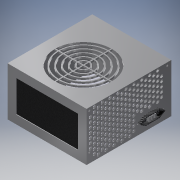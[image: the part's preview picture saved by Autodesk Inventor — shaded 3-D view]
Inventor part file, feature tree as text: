
AUTODESK INVENTOR PART (.ipt)
format: ipt  version: 2018.3 (Build 223284000, 284)  size: 2,151,424 bytes
history: native  units: mm
features: other x10, extrude x9, sketch x9, shell x1
ambient origin geometry x8: Origin, YZ Plane, XZ Plane, XY Plane, X Axis, Y Axis, Z Axis, Center Point
bodies: Solido1 (feature_tree)
feature tree (29):
  extrude  "Estrusione1"  Depth=140.0mm
  shell  "Svuotamento1"  Thickness=0.0mm
  extrude  "Estrusione2"  Depth=150.0mm
  extrude  "Estrusione3"  Depth=86.0mm TaperAngle=0.0deg
  extrude  "Estrusione4"  Depth=3.0mm
  extrude  "Estrusione5"  Depth=15.0mm
  extrude  "Estrusione6"  Depth=3.0mm TaperAngle=0.0deg
  extrude  "Estrusione7"  Depth=3.0mm
  extrude  "Estrusione8"  Depth=100.0mm
  extrude  "Estrusione9"  Depth=20.0mm
  sketch  "Schizzo1"
  sketch  "Schizzo3"
  other  "Linea chiusa proiettata1"
  sketch  "Schizzo4"
  sketch  "Schizzo5"
  other  "Linea chiusa proiettata2"
  sketch  "Schizzo6"
  sketch  "Schizzo7"
  other  "Linea chiusa proiettata3"
  other  "Linea chiusa proiettata4"
  other  "Linea chiusa proiettata5"
  other  "Linea chiusa proiettata6"
  sketch  "Schizzo8"
  sketch  "Schizzo9"
  sketch  "Schizzo10"
  other  "Linea chiusa proiettata7"
  other  "Proietta spigoli di taglio1"
  other  "Proietta spigoli di taglio2"
  other  "Proietta spigoli di taglio3"
